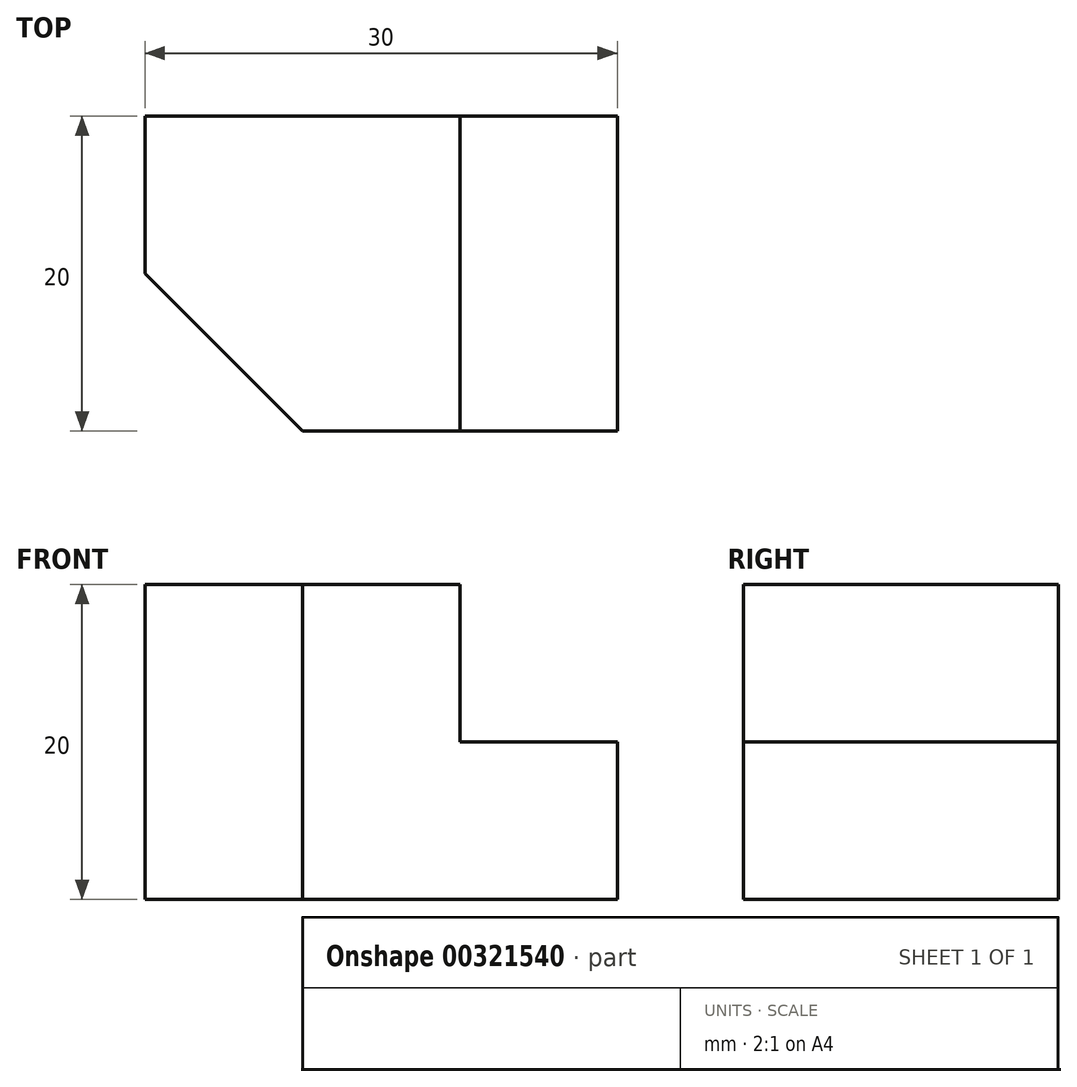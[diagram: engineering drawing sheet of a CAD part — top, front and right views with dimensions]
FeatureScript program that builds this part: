
annotation { "Feature Type Name" : "Feature", "Feature Type Description" : "" }
export const myFeature = defineFeature(function(context is Context, id is Id, definition is map)
    precondition{}
    {
        {
            var Q0;
            Q0=qCreatedBy(makeId("Front.planeOp"),FACE);
            var sketch = newSketch(context, id + "F0", { "sketchPlane" : qUnion([Q0])});
            skLineSegment(sketch, "E0", {"start": v(0, 0) * mm, "end": v(0, 20) * mm});
            skLineSegment(sketch, "E1", {"start": v(0, 20) * mm, "end": v(10, 20) * mm});
            skLineSegment(sketch, "E2", {"start": v(10, 20) * mm, "end": v(10, 0) * mm});
            skLineSegment(sketch, "E3", {"start": v(10, 0) * mm, "end": v(0, 0) * mm});
            skLineSegment(sketch, "E4", {"start": v(10, 20) * mm, "end": v(20, 20) * mm});
            skLineSegment(sketch, "E5", {"start": v(20, 20) * mm, "end": v(20, 10) * mm});
            skLineSegment(sketch, "E6", {"start": v(20, 10) * mm, "end": v(30, 10) * mm});
            skLineSegment(sketch, "E7", {"start": v(30, 10) * mm, "end": v(30, 0) * mm});
            skLineSegment(sketch, "E8", {"start": v(30, 0) * mm, "end": v(10, 0) * mm});
            skSolve(sketch);
        }
        {
            var Q0;
            Q0=makeQuery(id+"F0.imprint","IMPRINT",FACE,{"disambiguationData":[TD([[makeQuery(id+"F0.imprint","IMPRINT",EDGE,{"derivedFrom":sQuery(id+"F0.wireOp",EDGE,"E2")}),1.0]])]});
            extrude(context, id + "F1", {"entities" : qUnion([Q0]), "depth" : 20 * mm});
        }
        {
            var Q0;
            Q0=makeQuery(id+"F0.imprint","IMPRINT",FACE,{"disambiguationData":[TD([[makeQuery(id+"F0.imprint","IMPRINT",EDGE,{"derivedFrom":sQuery(id+"F0.wireOp",EDGE,"E0")}),-1.0]])]});
            extrude(context, id + "F2", {"entities" : qUnion([Q0]), "operationType" : NewBodyOperationType.ADD, "depth" : 20 * mm});
        }
        {
            var Q0;
            Q0=makeQuery(id+"F2.boolean.opBoolean","MERGE",FACE,{"derivedFrom":[makeQuery(id+"F1.opExtrude","SWEPT_FACE",FACE,{"disambiguationData":[OSD([sQuery(id+"F0.wireOp",EDGE,"E4")])]}),makeQuery(id+"F2.opExtrude","SWEPT_FACE",FACE,{"disambiguationData":[OSD([sQuery(id+"F0.wireOp",EDGE,"E1")])]})]});
            var sketch = newSketch(context, id + "F3", { "sketchPlane" : qUnion([Q0])});
            skLineSegment(sketch, "E9", {"start": v(0, -20) * mm, "end": v(0, -10) * mm});
            skLineSegment(sketch, "E10", {"start": v(0, -10) * mm, "end": v(10, -20) * mm});
            skLineSegment(sketch, "E11", {"start": v(10, -20) * mm, "end": v(0, -20) * mm});
            skSolve(sketch);
        }
        {
            var Q0;
            Q0=makeQuery(id+"F3.imprint","IMPRINT",FACE,{"disambiguationData":[TD([[makeQuery(id+"F3.imprint","IMPRINT",EDGE,{"derivedFrom":sQuery(id+"F3.wireOp",EDGE,"E9")}),-1.0]])]});
            extrude(context, id + "F4", {"entities" : qUnion([Q0]), "operationType" : NewBodyOperationType.REMOVE, "endBound" : BoundingType.THROUGH_ALL, "oppositeDirection" : true, "depth" : 25 * mm});
        }
    });
